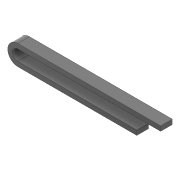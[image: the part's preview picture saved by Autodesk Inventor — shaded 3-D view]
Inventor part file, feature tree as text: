
AUTODESK INVENTOR PART (.ipt)
format: ipt  version: 2020 (Build 240168000, 168)  size: 99,840 bytes
history: native  units: mm
features: extrude x1, sketch x1
ambient origin geometry x8: Origin, YZ Plane, XZ Plane, XY Plane, X Axis, Y Axis, Z Axis, Center Point
bodies: Solid1 (feature_tree)
feature tree (2):
  extrude  "Extrusion1"  Depth=20.0mm
  sketch  "Sketch1"  dims[d0=85.0mm d1=20.0mm d2=20.0mm d4=500.0mm d5=49.0mm d6=0.0mm d9=600.0mm]
